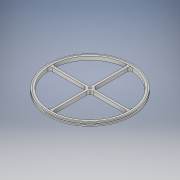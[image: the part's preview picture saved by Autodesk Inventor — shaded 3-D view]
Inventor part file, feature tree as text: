
AUTODESK INVENTOR PART (.ipt)
format: ipt  version: 2018 (Build 220112000, 112)  size: 224,256 bytes
history: native  units: in
note: dims shown in document units (in); Inventor stores cm internally (conversion verified against a paired STEP export)
features: extrude x8, sketch x8, fillet x2
ambient origin geometry x8: Origin, YZ Plane, XZ Plane, XY Plane, X Axis, Y Axis, Z Axis, Center Point
bodies: Solid1 (feature_tree)
feature tree (18):
  extrude  "Extrusion1"  Depth=4.849in
  extrude  "Extrusion2"  Depth=0.0625in
  extrude  "Extrusion3"  Depth=0.0625in TaperAngle=0.0deg
  extrude  "Extrusion4"  Depth=0.204in
  extrude  "Extrusion5"  Depth=0.204in
  extrude  "Extrusion6"  Depth=0.125in
  extrude  "Extrusion7"  Depth=0.204in TaperAngle=0.0deg
  fillet  "Fillet1"  Radius=0.125in
  fillet  "Fillet2"  Radius=0.125in
  extrude  "Extrusion8"  [1 undecoded]
  sketch  "Sketch1"  dims[d0=4.7244in d1=4.849in]
  sketch  "Sketch2"  dims[d2=0.0625in d3=0.0in d4=4.5in]
  sketch  "Sketch3"  dims[d5=0.0787in d6=0.0in d7=0.0625in d8=0.0in]
  sketch  "Sketch4"  dims[d9=0.204in d10=0.0in d11=4.5in]
  sketch  "Sketch5"  dims[d12=0.204in d13=0.0in d14=0.195in]
  sketch  "Sketch6"  dims[d15=0.204in d16=0.0in d17=0.125in]
  sketch  "Sketch7"  dims[d18=0.125in d19=0.204in d20=0.0in d21=0.125in d22=0.125in]
  sketch  "Sketch8"  dims[d23=0.204in d24=0.0in]
note: 1 required parameter value undecoded (feature->parameter linkage not recoverable at this tier; creation-order binding heuristic only, values carry confidence <= 0.55)
